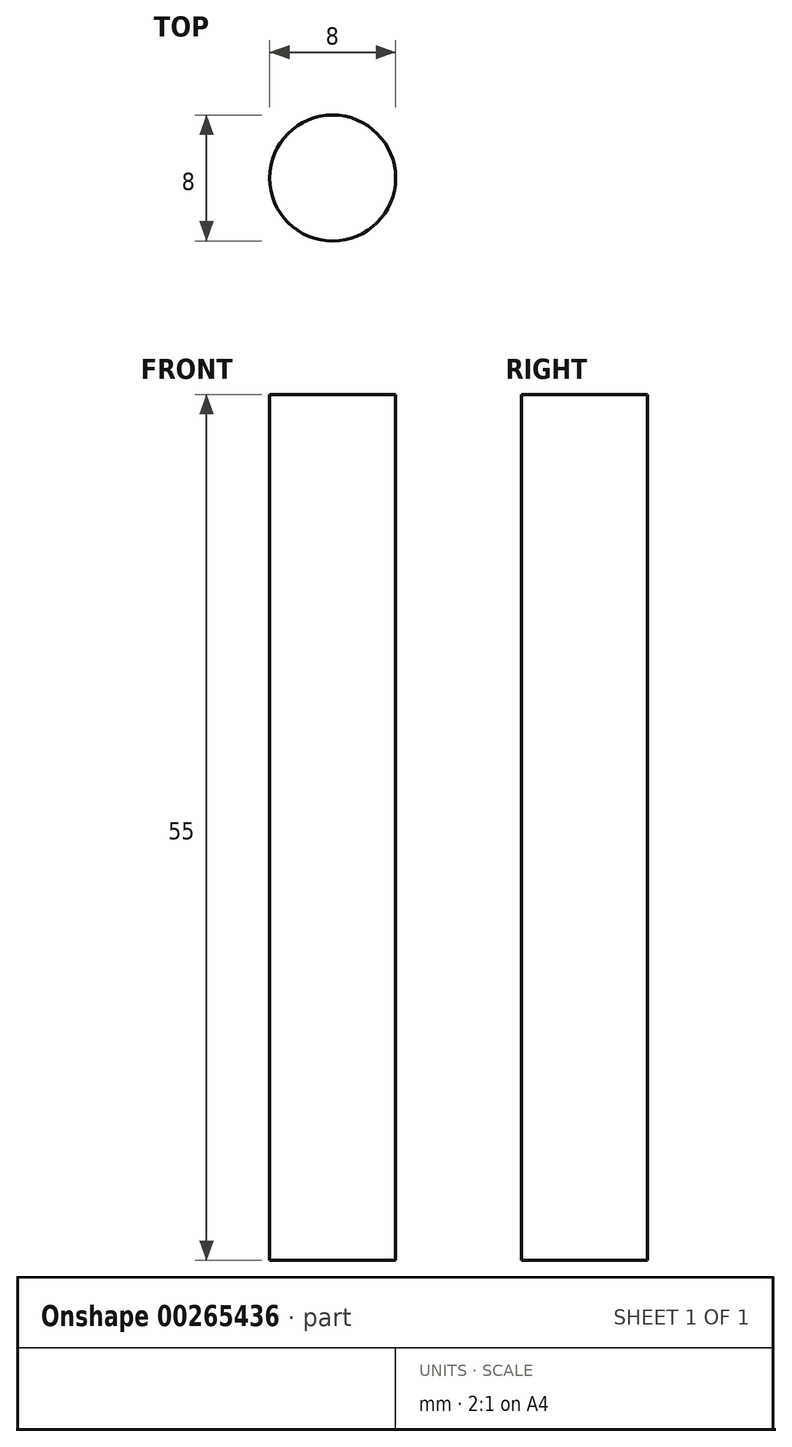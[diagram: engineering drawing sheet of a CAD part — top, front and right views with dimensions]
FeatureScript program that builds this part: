
annotation { "Feature Type Name" : "Feature", "Feature Type Description" : "" }
export const myFeature = defineFeature(function(context is Context, id is Id, definition is map)
    precondition{}
    {
        {
            var Q0;
            Q0=qCreatedBy(makeId("Top.planeOp"),FACE);
            cPlane(context, id + "F0", {"entities" : qUnion([Q0]), "cplaneType" : CPlaneType.OFFSET, "offset" : 55 * mm, "width" : 150 * mm, "height" : 150 * mm});
        }
        {
            var Q0;
            Q0=qCreatedBy(id+"F0.planeOp",FACE);
            var sketch = newSketch(context, id + "F1", { "sketchPlane" : qUnion([Q0])});
            skCircle(sketch, "E0", {"center": v(0, 0) * mm, "radius": 4 * mm});
            skPoint(sketch, "E0.first.point", {"position": v(-4, 0) * mm});
            skPoint(sketch, "E0.second.point", {"position": v(4, 0) * mm});
            skPoint(sketch, "E0.third.point", {"position": v(0, 4) * mm});
            skSolve(sketch);
        }
        {
            var Q0;
            Q0=qCreatedBy(makeId("Top.planeOp"),FACE);
            var sketch = newSketch(context, id + "F2", { "sketchPlane" : qUnion([Q0])});
            skCircle(sketch, "E1", {"center": v(0, 0) * mm, "radius": 4 * mm});
            skPoint(sketch, "E1.first.point", {"position": v(-4, 0) * mm});
            skPoint(sketch, "E1.second.point", {"position": v(0, 4) * mm});
            skPoint(sketch, "E1.third.point", {"position": v(4, 0) * mm});
            skSolve(sketch);
        }
        {
            var Q0;
            Q0=makeQuery(id+"F1.imprint","IMPRINT",FACE,{"disambiguationData":[TD([[makeQuery(id+"F1.imprint","IMPRINT",EDGE,{"derivedFrom":sQuery(id+"F1.wireOp",EDGE,"E0")}),1.0]])]});
            var Q1;
            Q1=makeQuery(id+"F2.imprint","IMPRINT",FACE,{"disambiguationData":[TD([[makeQuery(id+"F2.imprint","IMPRINT",EDGE,{"derivedFrom":sQuery(id+"F2.wireOp",EDGE,"E1")}),1.0]])]});
            loft(context, id + "F3", {"sheetProfilesArray" : [{ "sheetProfileEntities" : qUnion([Q0]) }, { "sheetProfileEntities" : qUnion([Q1]) }]});
        }
    });
